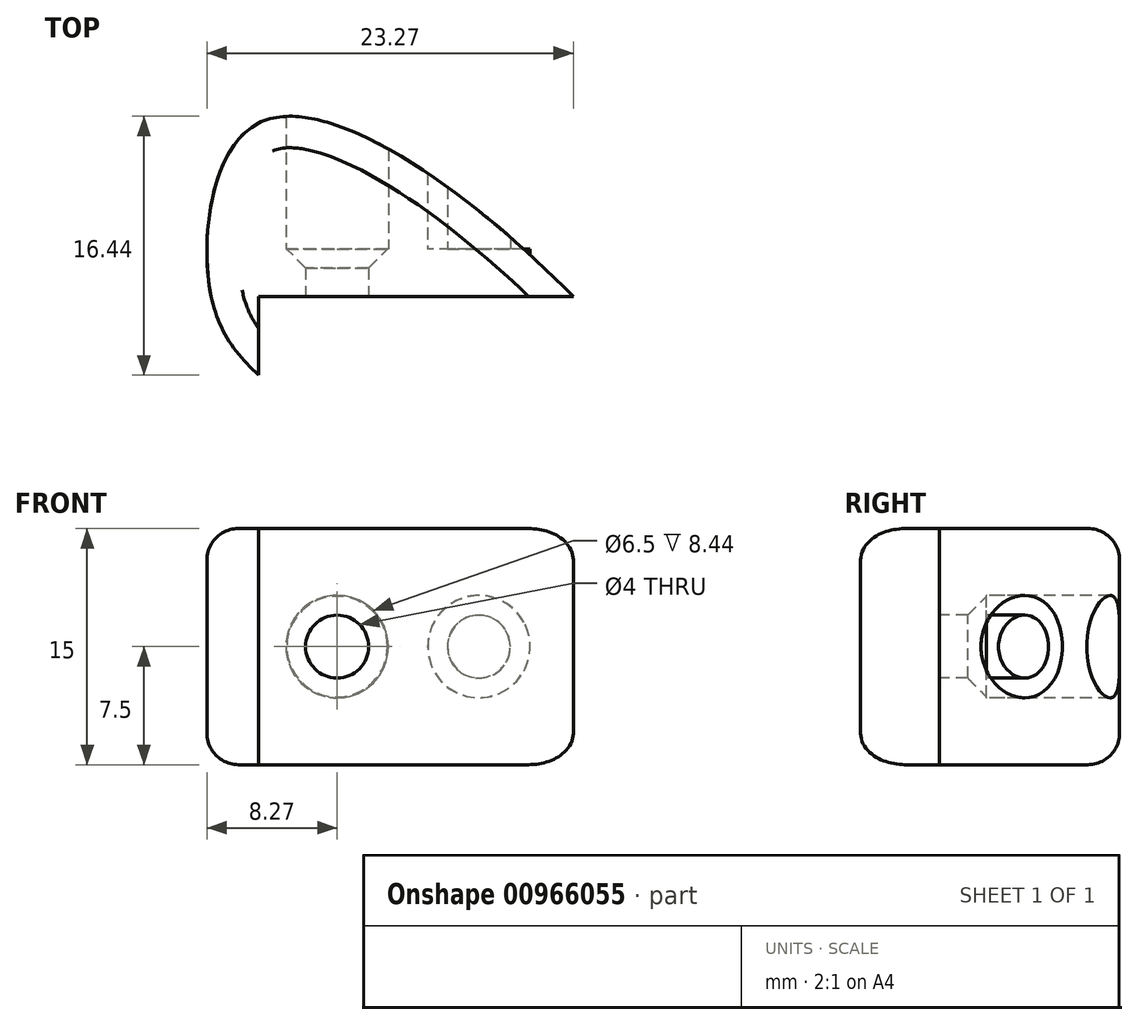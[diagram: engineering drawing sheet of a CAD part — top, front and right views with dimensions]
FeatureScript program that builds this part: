
annotation { "Feature Type Name" : "Feature", "Feature Type Description" : "" }
export const myFeature = defineFeature(function(context is Context, id is Id, definition is map)
    precondition{}
    {
        {
            var Q0;
            Q0=qCreatedBy(makeId("Top.planeOp"),FACE);
            var sketch = newSketch(context, id + "F0", { "sketchPlane" : qUnion([Q0])});
            skLineSegment(sketch, "E0", {"start": v(0, 0) * mm, "end": v(0, -5) * mm});
            skLineSegment(sketch, "E1", {"start": v(0, 0) * mm, "end": v(0, 11) * mm});
            skLineSegment(sketch, "E2", {"start": v(0, 0) * mm, "end": v(-3, 0) * mm});
            skLineSegment(sketch, "E3.bottom", {"start": v(0, 0) * mm, "end": v(20, 0) * mm});
            skLineSegment(sketch, "E3.top", {"start": v(0, 11) * mm, "end": v(20, 11) * mm});
            skLineSegment(sketch, "E3.right", {"start": v(20, 0) * mm, "end": v(20, 11) * mm});
            skFitSpline(sketch, "E4", {"points": [v(20, 0) * mm, v(0, 11) * mm, v(-3, 0) * mm, v(0, -5) * mm], "startDerivative": vector(-43.57, 44.26) * mm, "endDerivative": vector(16.16, -15.59) * mm});
            skSolve(sketch);
        }
        {
            var Q0;
            {var subQ0=sQuery(id+"F0.wireOp",EDGE,"E4");var subQ1=sQuery(id+"F0.wireOp",EDGE,"E3.top");var subQ3=makeQuery(id+"F0.imprint","INTERSECT",VERTEX,{"derivedFrom":[subQ1,subQ0]});Q0=makeQuery(id+"F0.imprint","IMPRINT",FACE,{"disambiguationData":[TD([[makeQuery(id+"F0.imprint","IMPRINT",EDGE,{"disambiguationData":[TD([[subQ3,1.0]])],"derivedFrom":subQ1}),1.0]])]});}
            var Q1;
            {var subQ0=sQuery(id+"F0.wireOp",EDGE,"E1");Q1=makeQuery(id+"F0.imprint","IMPRINT",FACE,{"disambiguationData":[TD([[makeQuery(id+"F0.imprint","IMPRINT",EDGE,{"derivedFrom":subQ0}),-1.0]])]});}
            var Q2;
            {var subQ0=sQuery(id+"F0.wireOp",EDGE,"E1");Q2=makeQuery(id+"F0.imprint","IMPRINT",FACE,{"disambiguationData":[TD([[makeQuery(id+"F0.imprint","IMPRINT",EDGE,{"derivedFrom":subQ0}),1.0]])]});}
            var Q3;
            {var subQ0=sQuery(id+"F0.wireOp",EDGE,"E0");Q3=makeQuery(id+"F0.imprint","IMPRINT",FACE,{"disambiguationData":[TD([[makeQuery(id+"F0.imprint","IMPRINT",EDGE,{"derivedFrom":subQ0}),-1.0]])]});}
            extrude(context, id + "F1", {"entities" : qUnion([Q0, Q1, Q2, Q3]), "depth" : 15 * mm, "offsetDistance" : 25 * mm});
        }
        {
            var Q0;
            Q0=makeQuery(id+"F1.opExtrude","SWEPT_FACE",FACE,{"disambiguationData":[OSD([sQuery(id+"F0.wireOp",EDGE,"E3.bottom")])]});
            var sketch = newSketch(context, id + "F2", { "sketchPlane" : qUnion([Q0])});
            skLineSegment(sketch, "E5", {"start": v(0, 7.5) * mm, "end": v(20, 7.5) * mm});
            skPoint(sketch, "E6", {"position": v(5, 7.5) * mm});
            skPoint(sketch, "E7", {"position": v(14, 7.5) * mm});
            skCircle(sketch, "E8", {"center": v(5, 7.5) * mm, "radius": 2 * mm});
            skCircle(sketch, "E9", {"center": v(14, 7.5) * mm, "radius": 2 * mm});
            skCircle(sketch, "E10", {"center": v(5, 7.5) * mm, "radius": 3.25 * mm});
            skCircle(sketch, "E11", {"center": v(14, 7.5) * mm, "radius": 3.25 * mm});
            skSolve(sketch);
        }
        {
            var Q0;
            {var subQ0=sQuery(id+"F2.wireOp",EDGE,"E8");var subQ1=sQuery(id+"F2.wireOp",EDGE,"E5");var subQ2=makeQuery(id+"F2.imprint","INTERSECT",VERTEX,{"disambiguationData":[OD(0.0)],"derivedFrom":[subQ1,subQ0]});Q0=makeQuery(id+"F2.imprint","IMPRINT",FACE,{"disambiguationData":[TD([[makeQuery(id+"F2.imprint","IMPRINT",EDGE,{"disambiguationData":[TD([[subQ2,-1.0]])],"derivedFrom":subQ1}),1.0]])]});}
            var Q1;
            {var subQ0=sQuery(id+"F2.wireOp",EDGE,"E8");var subQ1=sQuery(id+"F2.wireOp",EDGE,"E5");var subQ2=makeQuery(id+"F2.imprint","INTERSECT",VERTEX,{"disambiguationData":[OD(0.0)],"derivedFrom":[subQ1,subQ0]});Q1=makeQuery(id+"F2.imprint","IMPRINT",FACE,{"disambiguationData":[TD([[makeQuery(id+"F2.imprint","IMPRINT",EDGE,{"disambiguationData":[TD([[subQ2,-1.0]])],"derivedFrom":subQ1}),-1.0]])]});}
            var Q2;
            {var subQ0=sQuery(id+"F2.wireOp",EDGE,"E9");var subQ1=sQuery(id+"F2.wireOp",EDGE,"E5");var subQ2=makeQuery(id+"F2.imprint","INTERSECT",VERTEX,{"disambiguationData":[OD(0.0)],"derivedFrom":[subQ1,subQ0]});Q2=makeQuery(id+"F2.imprint","IMPRINT",FACE,{"disambiguationData":[TD([[makeQuery(id+"F2.imprint","IMPRINT",EDGE,{"disambiguationData":[TD([[subQ2,1.0]])],"derivedFrom":subQ1}),1.0]])]});}
            var Q3;
            {var subQ0=sQuery(id+"F2.wireOp",EDGE,"E9");var subQ1=sQuery(id+"F2.wireOp",EDGE,"E5");var subQ2=makeQuery(id+"F2.imprint","INTERSECT",VERTEX,{"disambiguationData":[OD(0.0)],"derivedFrom":[subQ1,subQ0]});Q3=makeQuery(id+"F2.imprint","IMPRINT",FACE,{"disambiguationData":[TD([[makeQuery(id+"F2.imprint","IMPRINT",EDGE,{"disambiguationData":[TD([[subQ2,1.0]])],"derivedFrom":subQ1}),-1.0]])]});}
            extrude(context, id + "F3", {"entities" : qUnion([Q0, Q1, Q2, Q3]), "operationType" : NewBodyOperationType.REMOVE, "oppositeDirection" : true, "depth" : 25 * mm, "offsetDistance" : 25 * mm});
        }
        {
            var Q0;
            Q0 = qSketchRegion(id + "F2", true);
            extrude(context, id + "F4", {"entities" : qUnion([Q0]), "operationType" : NewBodyOperationType.REMOVE, "oppositeDirection" : true, "depth" : 25 * mm, "offsetDistance" : 25 * mm});
        }
        {
            var Q0;
            Q0 = qSketchRegion(id + "F2", true);
            extrude(context, id + "F5", {"entities" : qUnion([Q0]), "operationType" : NewBodyOperationType.ADD, "oppositeDirection" : true, "depth" : 3 * mm, "offsetDistance" : 25 * mm});
        }
        {
            var Q0;
            Q0=makeQuery(id+"F5.opExtrude","CAP_EDGE",EDGE,{"disambiguationData":[OSD([sQuery(id+"F2.wireOp",EDGE,"E8")])],"isStart":false});
            var Q1;
            Q1=makeQuery(id+"F5.opExtrude","CAP_EDGE",EDGE,{"disambiguationData":[OSD([sQuery(id+"F2.wireOp",EDGE,"E9")])],"isStart":false});
            chamfer(context, id + "F6", {"entities" : qUnion([Q0, Q1]), "width" : 1.2 * mm, "tangentPropagation" : true});
        }
        {
            var Q0;
            {var subQ0=sQuery(id+"F0.wireOp",EDGE,"E4");Q0=makeQuery(id+"F1.opExtrude","CAP_EDGE",EDGE,{"disambiguationData":[OSD([subQ0]),TDD([makeQuery(id+"F0.imprint","IMPRINT",EDGE,{"disambiguationData":[TD([[makeQuery(id+"F0.imprint","INTERSECT",VERTEX,{"derivedFrom":[sQuery(id+"F0.wireOp",EDGE,"E2"),subQ0]}),1.0]])],"derivedFrom":subQ0})])],"isStart":true});}
            var Q1;
            {var subQ0=sQuery(id+"F0.wireOp",EDGE,"E4");Q1=makeQuery(id+"F1.opExtrude","CAP_EDGE",EDGE,{"disambiguationData":[OSD([subQ0]),TDD([makeQuery(id+"F0.imprint","IMPRINT",EDGE,{"disambiguationData":[TD([[makeQuery(id+"F0.imprint","INTERSECT",VERTEX,{"derivedFrom":[sQuery(id+"F0.wireOp",EDGE,"E0"),subQ0]}),1.0]])],"derivedFrom":subQ0})])],"isStart":true});}
            var Q2;
            {var subQ0=sQuery(id+"F0.wireOp",EDGE,"E4");var subQ1=sQuery(id+"F0.wireOp",EDGE,"E3.top");Q2=makeQuery(id+"F1.opExtrude","CAP_EDGE",EDGE,{"disambiguationData":[OSD([subQ0]),TDD([makeQuery(id+"F0.imprint","IMPRINT",EDGE,{"disambiguationData":[TD([[makeQuery(id+"F0.imprint","INTERSECT",VERTEX,{"derivedFrom":[subQ1,subQ0]}),-1.0]])],"derivedFrom":subQ0})])],"isStart":true});}
            var Q3;
            {var subQ0=sQuery(id+"F0.wireOp",EDGE,"E4");Q3=makeQuery(id+"F1.opExtrude","CAP_EDGE",EDGE,{"disambiguationData":[OSD([subQ0]),TDD([makeQuery(id+"F0.imprint","IMPRINT",EDGE,{"disambiguationData":[TD([[makeQuery(id+"F0.imprint","INTERSECT",VERTEX,{"derivedFrom":[sQuery(id+"F0.wireOp",EDGE,"E3.top"),subQ0]}),1.0]])],"derivedFrom":subQ0})])],"isStart":true});}
            var Q4;
            {var subQ0=sQuery(id+"F0.wireOp",EDGE,"E4");Q4=makeQuery(id+"F1.opExtrude","CAP_EDGE",EDGE,{"disambiguationData":[OSD([subQ0]),TDD([makeQuery(id+"F0.imprint","IMPRINT",EDGE,{"disambiguationData":[TD([[makeQuery(id+"F0.imprint","INTERSECT",VERTEX,{"derivedFrom":[sQuery(id+"F0.wireOp",EDGE,"E2"),subQ0]}),1.0]])],"derivedFrom":subQ0})])],"isStart":false});}
            var Q5;
            {var subQ0=sQuery(id+"F0.wireOp",EDGE,"E4");var subQ1=sQuery(id+"F0.wireOp",EDGE,"E3.top");Q5=makeQuery(id+"F1.opExtrude","CAP_EDGE",EDGE,{"disambiguationData":[OSD([subQ0]),TDD([makeQuery(id+"F0.imprint","IMPRINT",EDGE,{"disambiguationData":[TD([[makeQuery(id+"F0.imprint","INTERSECT",VERTEX,{"derivedFrom":[subQ1,subQ0]}),-1.0]])],"derivedFrom":subQ0})])],"isStart":false});}
            fillet(context, id + "F7", {"entities" : qUnion([Q0, Q1, Q2, Q3, Q4, Q5]), "tangentPropagation" : true, "radius" : 2 * mm, "defaultsChanged" : false, "vertexSettings" : [], "allowEdgeOverflow" : false});
        }
    });
